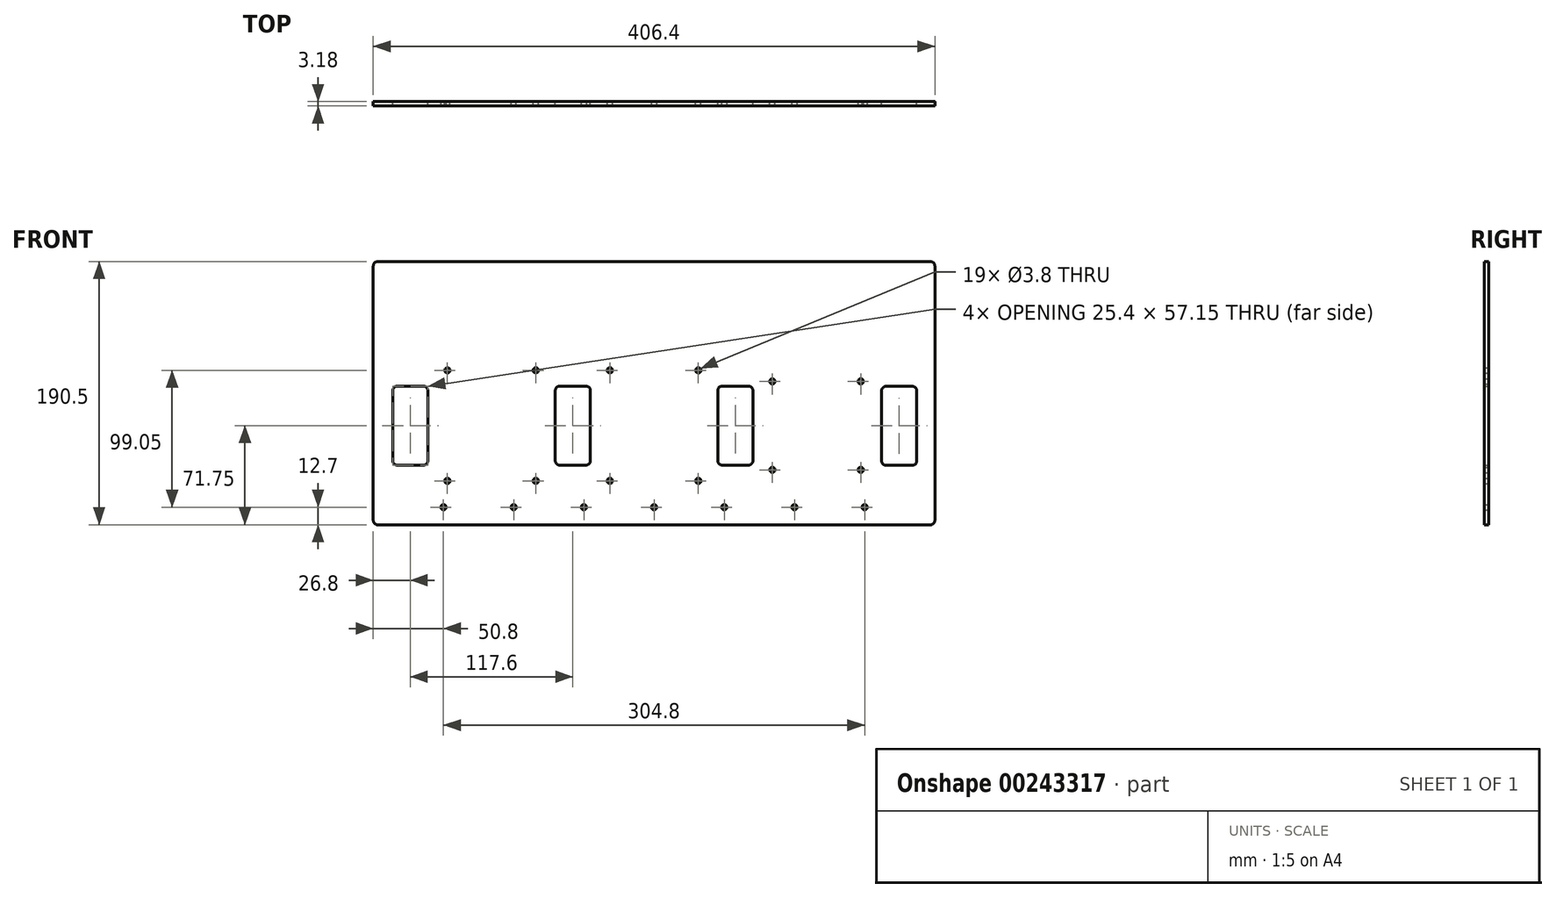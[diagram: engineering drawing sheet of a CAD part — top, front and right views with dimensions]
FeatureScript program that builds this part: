
annotation { "Feature Type Name" : "Feature", "Feature Type Description" : "" }
export const myFeature = defineFeature(function(context is Context, id is Id, definition is map)
    precondition{}
    {
        {
            var Q0;
            Q0=qCreatedBy(makeId("Front.planeOp"),FACE);
            var sketch = newSketch(context, id + "F0", { "sketchPlane" : qUnion([Q0])});
            skLineSegment(sketch, "E0.bottom", {"start": v(-200.03, 95.25) * mm, "end": v(200.03, 95.25) * mm});
            skLineSegment(sketch, "E0.top", {"start": v(-200.03, -95.25) * mm, "end": v(200.03, -95.25) * mm});
            skLineSegment(sketch, "E0.left", {"start": v(-203.2, 92.07) * mm, "end": v(-203.2, -92.07) * mm});
            skLineSegment(sketch, "E0.right", {"start": v(203.2, 92.07) * mm, "end": v(203.2, -92.07) * mm});
            skPoint(sketch, "E0.middle", {"position": v(0, 0) * mm});
            skCircle(sketch, "E1", {"center": v(-149.6, 16.5) * mm, "radius": 1.9 * mm});
            skCircle(sketch, "E2.MirrorC", {"center": v(-149.6, -63.5) * mm, "radius": 1.9 * mm});
            skCircle(sketch, "E3.2.0.3", {"center": v(-85.6, -63.5) * mm, "radius": 1.9 * mm});
            skCircle(sketch, "E3.3.0.0", {"center": v(-32, 16.5) * mm, "radius": 1.9 * mm});
            skCircle(sketch, "E3.3.0.2", {"center": v(-32, -63.5) * mm, "radius": 1.9 * mm});
            skCircle(sketch, "E3.5.0.0", {"center": v(32, 16.5) * mm, "radius": 1.9 * mm});
            skCircle(sketch, "E3.5.0.2", {"center": v(32, -63.5) * mm, "radius": 1.9 * mm});
            skLineSegment(sketch, "E4.bottom", {"start": v(-32, 16.5) * mm, "end": v(32, 16.5) * mm, "construction": true});
            skLineSegment(sketch, "E4.top", {"start": v(-32, -63.5) * mm, "end": v(32, -63.5) * mm});
            skLineSegment(sketch, "E4.left", {"start": v(-32, 16.5) * mm, "end": v(-32, -63.5) * mm, "construction": true});
            skLineSegment(sketch, "E4.right", {"start": v(32, 16.5) * mm, "end": v(32, -63.5) * mm, "construction": true});
            skLineSegment(sketch, "E5.bottom", {"start": v(-149.6, 16.5) * mm, "end": v(-85.6, 16.5) * mm, "construction": true});
            skLineSegment(sketch, "E5.top", {"start": v(-149.6, -63.5) * mm, "end": v(-85.6, -63.5) * mm, "construction": true});
            skLineSegment(sketch, "E5.left", {"start": v(-149.6, 16.5) * mm, "end": v(-149.6, -63.5) * mm, "construction": true});
            skLineSegment(sketch, "E5.right", {"start": v(-85.6, 16.5) * mm, "end": v(-85.6, -63.5) * mm, "construction": true});
            skCircle(sketch, "E6", {"center": v(-85.6, 16.5) * mm, "radius": 1.9 * mm});
            skLineSegment(sketch, "E7", {"start": v(-203.2, -82.55) * mm, "end": v(-152.4, -82.55) * mm, "construction": true});
            skCircle(sketch, "E8", {"center": v(-152.4, -82.55) * mm, "radius": 1.9 * mm});
            skCircle(sketch, "E9.1.0.0", {"center": v(-101.6, -82.55) * mm, "radius": 1.9 * mm});
            skCircle(sketch, "E9.2.0.0", {"center": v(-50.8, -82.55) * mm, "radius": 1.9 * mm});
            skCircle(sketch, "E9.3.0.0", {"center": v(0, -82.55) * mm, "radius": 1.9 * mm});
            skCircle(sketch, "E9.4.0.0", {"center": v(50.8, -82.55) * mm, "radius": 1.9 * mm});
            skCircle(sketch, "E9.5.0.0", {"center": v(101.6, -82.55) * mm, "radius": 1.9 * mm});
            skCircle(sketch, "E9.6.0.0", {"center": v(152.4, -82.55) * mm, "radius": 1.9 * mm});
            skLineSegment(sketch, "E9.direction1", {"start": v(-152.4, -82.55) * mm, "end": v(-101.6, -82.55) * mm, "construction": true});
            skLineSegment(sketch, "E10", {"start": v(-85.6, -63.5) * mm, "end": v(203.2, -63.5) * mm, "construction": true});
            skLineSegment(sketch, "E11", {"start": v(-85.6, -23.5) * mm, "end": v(-32, -23.5) * mm, "construction": true});
            skLineSegment(sketch, "E12", {"start": v(32, -23.5) * mm, "end": v(85.6, -23.5) * mm, "construction": true});
            skLineSegment(sketch, "E13", {"start": v(-149.6, -23.5) * mm, "end": v(-203.2, -23.5) * mm, "construction": true});
            skLineSegment(sketch, "E14", {"start": v(149.6, -23.5) * mm, "end": v(203.2, -23.5) * mm, "construction": true});
            skLineSegment(sketch, "E15.bottom", {"start": v(-201.9, 95.25) * mm, "end": v(52.1, 95.25) * mm, "construction": true});
            skLineSegment(sketch, "E15.top", {"start": v(-201.9, 19.05) * mm, "end": v(52.1, 19.05) * mm, "construction": true});
            skLineSegment(sketch, "E15.left", {"start": v(-201.9, 95.25) * mm, "end": v(-201.9, 19.05) * mm, "construction": true});
            skLineSegment(sketch, "E15.right", {"start": v(52.1, 95.25) * mm, "end": v(52.1, 19.05) * mm, "construction": true});
            skPoint(sketch, "E15.middle", {"position": v(-74.9, 57.15) * mm});
            skLineSegment(sketch, "E16.bottom", {"start": v(-185.93, 5.07) * mm, "end": v(-166.88, 5.07) * mm});
            skLineSegment(sketch, "E16.top", {"start": v(-185.93, -52.08) * mm, "end": v(-166.88, -52.08) * mm});
            skLineSegment(sketch, "E16.left", {"start": v(-189.1, 1.9) * mm, "end": v(-189.1, -48.9) * mm});
            skLineSegment(sketch, "E16.right", {"start": v(-163.7, 1.9) * mm, "end": v(-163.7, -48.9) * mm});
            skPoint(sketch, "E16.middle", {"position": v(-176.4, -23.5) * mm});
            skLineSegment(sketch, "E17.bottom", {"start": v(-68.33, 5.07) * mm, "end": v(-49.28, 5.07) * mm});
            skLineSegment(sketch, "E17.top", {"start": v(-68.33, -52.08) * mm, "end": v(-49.28, -52.08) * mm});
            skLineSegment(sketch, "E17.left", {"start": v(-71.5, 1.9) * mm, "end": v(-71.5, -48.9) * mm});
            skLineSegment(sketch, "E17.right", {"start": v(-46.1, 1.9) * mm, "end": v(-46.1, -48.9) * mm});
            skPoint(sketch, "E17.middle", {"position": v(-58.8, -23.5) * mm});
            skLineSegment(sketch, "E18.bottom", {"start": v(49.28, 5.07) * mm, "end": v(68.32, 5.07) * mm});
            skLineSegment(sketch, "E18.top", {"start": v(49.28, -52.08) * mm, "end": v(68.32, -52.08) * mm});
            skLineSegment(sketch, "E18.left", {"start": v(46.1, 1.9) * mm, "end": v(46.1, -48.9) * mm});
            skLineSegment(sketch, "E18.right", {"start": v(71.5, 1.9) * mm, "end": v(71.5, -48.9) * mm});
            skPoint(sketch, "E18.middle", {"position": v(58.8, -23.5) * mm});
            skPoint(sketch, "E19.visualSharp", {"position": v(-203.2, 95.25) * mm});
            skArc(sketch, "E19.filletArc", {"start": v(-200.03, 95.25) * mm, "mid": v(-202.27, 94.32) * mm, "end": v(-203.2, 92.07) * mm});
            skPoint(sketch, "E20.visualSharp", {"position": v(203.2, 95.25) * mm});
            skArc(sketch, "E20.filletArc", {"start": v(203.2, 92.07) * mm, "mid": v(202.27, 94.32) * mm, "end": v(200.03, 95.25) * mm});
            skArc(sketch, "E21.filletArc", {"start": v(71.5, 1.9) * mm, "mid": v(70.57, 4.15) * mm, "end": v(68.32, 5.08) * mm});
            skPoint(sketch, "E22.visualSharp", {"position": v(46.1, 5.07) * mm});
            skArc(sketch, "E22.filletArc", {"start": v(49.28, 5.08) * mm, "mid": v(47.03, 4.15) * mm, "end": v(46.1, 1.9) * mm});
            skArc(sketch, "E23.filletArc", {"start": v(68.32, -52.08) * mm, "mid": v(70.57, -51.15) * mm, "end": v(71.5, -48.9) * mm});
            skPoint(sketch, "E24.visualSharp", {"position": v(46.1, -52.08) * mm});
            skArc(sketch, "E24.filletArc", {"start": v(46.1, -48.9) * mm, "mid": v(47.03, -51.15) * mm, "end": v(49.28, -52.08) * mm});
            skPoint(sketch, "E25.visualSharp", {"position": v(-46.1, -52.08) * mm});
            skArc(sketch, "E25.filletArc", {"start": v(-49.28, -52.08) * mm, "mid": v(-47.03, -51.15) * mm, "end": v(-46.1, -48.9) * mm});
            skPoint(sketch, "E26.visualSharp", {"position": v(-71.5, 5.07) * mm});
            skArc(sketch, "E26.filletArc", {"start": v(-68.33, 5.07) * mm, "mid": v(-70.57, 4.15) * mm, "end": v(-71.5, 1.9) * mm});
            skPoint(sketch, "E27.visualSharp", {"position": v(-46.1, 5.07) * mm});
            skArc(sketch, "E27.filletArc", {"start": v(-46.1, 1.9) * mm, "mid": v(-47.03, 4.15) * mm, "end": v(-49.28, 5.07) * mm});
            skPoint(sketch, "E28.visualSharp", {"position": v(-71.5, -52.08) * mm});
            skArc(sketch, "E28.filletArc", {"start": v(-71.5, -48.9) * mm, "mid": v(-70.57, -51.15) * mm, "end": v(-68.33, -52.08) * mm});
            skPoint(sketch, "E29.visualSharp", {"position": v(-163.7, -52.08) * mm});
            skArc(sketch, "E29.filletArc", {"start": v(-166.88, -52.07) * mm, "mid": v(-164.63, -51.15) * mm, "end": v(-163.7, -48.9) * mm});
            skPoint(sketch, "E30.visualSharp", {"position": v(-189.1, -52.08) * mm});
            skArc(sketch, "E30.filletArc", {"start": v(-189.1, -48.9) * mm, "mid": v(-188.17, -51.15) * mm, "end": v(-185.93, -52.07) * mm});
            skPoint(sketch, "E31.visualSharp", {"position": v(-189.1, 5.07) * mm});
            skArc(sketch, "E31.filletArc", {"start": v(-185.93, 5.07) * mm, "mid": v(-188.17, 4.15) * mm, "end": v(-189.1, 1.9) * mm});
            skPoint(sketch, "E32.visualSharp", {"position": v(-163.7, 5.07) * mm});
            skArc(sketch, "E32.filletArc", {"start": v(-163.7, 1.9) * mm, "mid": v(-164.63, 4.15) * mm, "end": v(-166.88, 5.07) * mm});
            skPoint(sketch, "E33.visualSharp", {"position": v(-203.2, -95.25) * mm});
            skArc(sketch, "E33.filletArc", {"start": v(-203.2, -92.07) * mm, "mid": v(-202.27, -94.32) * mm, "end": v(-200.03, -95.25) * mm});
            skPoint(sketch, "E34.visualSharp", {"position": v(203.2, -95.25) * mm});
            skArc(sketch, "E34.filletArc", {"start": v(200.03, -95.25) * mm, "mid": v(202.27, -94.32) * mm, "end": v(203.2, -92.07) * mm});
            skCircle(sketch, "E35", {"center": v(85.6, -55.5) * mm, "radius": 1.9 * mm});
            skCircle(sketch, "E36.MirrorC", {"center": v(85.6, 8.5) * mm, "radius": 1.9 * mm});
            skCircle(sketch, "E37.2.0.1", {"center": v(149.6, 8.5) * mm, "radius": 1.9 * mm});
            skCircle(sketch, "E37.2.0.3", {"center": v(149.6, -55.5) * mm, "radius": 1.9 * mm});
            skLineSegment(sketch, "E38.bottom", {"start": v(85.6, 8.5) * mm, "end": v(149.6, 8.5) * mm, "construction": true});
            skLineSegment(sketch, "E38.top", {"start": v(85.6, -55.5) * mm, "end": v(149.6, -55.5) * mm, "construction": true});
            skLineSegment(sketch, "E38.left", {"start": v(85.6, 8.5) * mm, "end": v(85.6, -55.5) * mm, "construction": true});
            skLineSegment(sketch, "E38.right", {"start": v(149.6, 8.5) * mm, "end": v(149.6, -55.5) * mm, "construction": true});
            skPoint(sketch, "E39.middle.positionSnap0", {"position": v(149.6, -23.5) * mm});
            skPoint(sketch, "E39.centerSnap0", {"position": v(149.6, -23.5) * mm});
            skLineSegment(sketch, "E40.bottom", {"start": v(167.87, 4.9) * mm, "end": v(186.92, 4.9) * mm});
            skLineSegment(sketch, "E40.top", {"start": v(167.87, -52.24) * mm, "end": v(186.92, -52.24) * mm});
            skLineSegment(sketch, "E40.left", {"start": v(164.7, 1.73) * mm, "end": v(164.7, -49.07) * mm});
            skLineSegment(sketch, "E40.right", {"start": v(190.1, 1.73) * mm, "end": v(190.1, -49.07) * mm});
            skPoint(sketch, "E40.middle", {"position": v(177.4, -23.67) * mm});
            skArc(sketch, "E41.filletArc", {"start": v(190.1, 1.73) * mm, "mid": v(189.16, 3.98) * mm, "end": v(186.92, 4.9) * mm});
            skPoint(sketch, "E42.visualSharp", {"position": v(164.7, 4.9) * mm});
            skArc(sketch, "E42.filletArc", {"start": v(167.87, 4.9) * mm, "mid": v(165.62, 3.98) * mm, "end": v(164.7, 1.73) * mm});
            skArc(sketch, "E43.filletArc", {"start": v(186.92, -52.24) * mm, "mid": v(189.16, -51.31) * mm, "end": v(190.1, -49.07) * mm});
            skPoint(sketch, "E44.visualSharp", {"position": v(164.7, -52.24) * mm});
            skArc(sketch, "E44.filletArc", {"start": v(164.7, -49.07) * mm, "mid": v(165.62, -51.31) * mm, "end": v(167.87, -52.24) * mm});
            skSolve(sketch);
        }
        {
            var Q0;
            Q0 = qSketchRegion(id + "F0", true);
            extrude(context, id + "F1", {"entities" : qUnion([Q0]), "depth" : 3.17 * mm});
        }
    });
